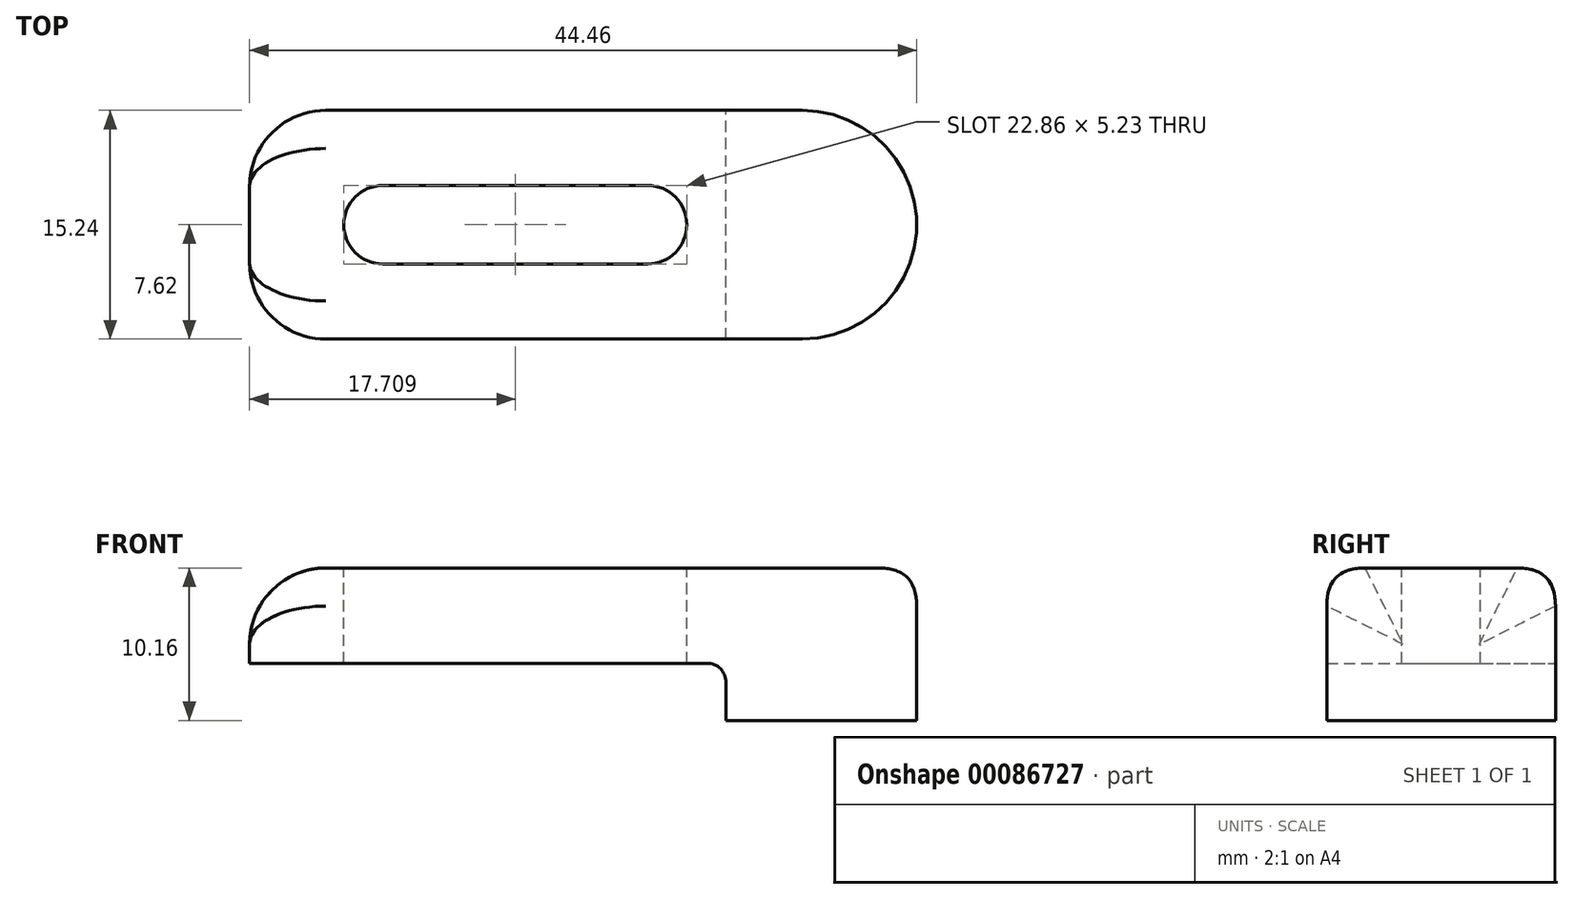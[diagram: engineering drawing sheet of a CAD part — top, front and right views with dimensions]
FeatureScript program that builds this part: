
annotation { "Feature Type Name" : "Feature", "Feature Type Description" : "" }
export const myFeature = defineFeature(function(context is Context, id is Id, definition is map)
    precondition{}
    {
        {
            var Q0;
            Q0=qCreatedBy(makeId("Top.planeOp"),FACE);
            var sketch = newSketch(context, id + "F0", { "sketchPlane" : qUnion([Q0])});
            skLineSegment(sketch, "E0.bottom", {"start": v(14.6, -7.62) * mm, "end": v(-22.23, -7.62) * mm});
            skLineSegment(sketch, "E0.top", {"start": v(14.6, 7.62) * mm, "end": v(-22.23, 7.62) * mm});
            skLineSegment(sketch, "E0.left", {"start": v(22.23, 0) * mm, "end": v(22.23, 0) * mm});
            skLineSegment(sketch, "E0.right", {"start": v(-22.23, -7.62) * mm, "end": v(-22.23, 7.62) * mm});
            skPoint(sketch, "E0.middle", {"position": v(0, 0) * mm});
            skPoint(sketch, "E1.visualSharp", {"position": v(22.23, 7.62) * mm});
            skArc(sketch, "E1.filletArc", {"start": v(22.23, 0) * mm, "mid": v(20, 5.39) * mm, "end": v(14.6, 7.62) * mm});
            skPoint(sketch, "E2.visualSharp", {"position": v(22.23, -7.62) * mm});
            skArc(sketch, "E2.filletArc", {"start": v(14.6, -7.62) * mm, "mid": v(20, -5.39) * mm, "end": v(22.23, 0) * mm});
            skSolve(sketch);
        }
        {
            var Q0;
            Q0=qSketchRegion(id+"F0",true);
            extrude(context, id + "F1", {"entities" : qUnion([Q0]), "depth" : 10.16 * mm});
        }
        {
            var Q0;
            Q0=makeQuery(id+"F1.opExtrude","CAP_FACE",FACE,{"disambiguationData":[OSD([sQuery(id+"F0.wireOp",EDGE,"E0.bottom"),sQuery(id+"F0.wireOp",EDGE,"E0.top"),sQuery(id+"F0.wireOp",EDGE,"E0.right"),sQuery(id+"F0.wireOp",EDGE,"E1.filletArc"),sQuery(id+"F0.wireOp",EDGE,"E2.filletArc")])],"isStart":true});
            var sketch = newSketch(context, id + "F2", { "sketchPlane" : qUnion([Q0])});
            skLineSegment(sketch, "E3.bottom", {"start": v(-22.23, 7.62) * mm, "end": v(9.53, 7.62) * mm});
            skLineSegment(sketch, "E3.top", {"start": v(-22.23, -7.62) * mm, "end": v(9.53, -7.62) * mm});
            skLineSegment(sketch, "E3.left", {"start": v(-22.23, 7.62) * mm, "end": v(-22.23, -7.62) * mm});
            skLineSegment(sketch, "E3.right", {"start": v(9.53, 7.62) * mm, "end": v(9.53, -7.62) * mm});
            skSolve(sketch);
        }
        {
            var Q0;
            Q0=qSketchRegion(id+"F2",true);
            extrude(context, id + "F3", {"entities" : qUnion([Q0]), "operationType" : NewBodyOperationType.REMOVE, "oppositeDirection" : true, "depth" : 3.8 * mm});
        }
        {
            var Q0;
            Q0=makeQuery(id+"F1.opExtrude","CAP_EDGE",EDGE,{"disambiguationData":[OSD([sQuery(id+"F0.wireOp",EDGE,"E0.bottom")])],"isStart":false});
            fillet(context, id + "F4", {"entities" : qUnion([Q0]), "radius" : 2.54 * mm, "tangentPropagation" : true, "rho" : 0.5, "crossSection" : FilletCrossSection.CONIC, "allowEdgeOverflow" : false});
        }
        {
            var Q0;
            Q0=makeQuery(id+"F3.boolean.opBoolean","COPY",EDGE,{"derivedFrom":makeQuery(id+"F3.opExtrude","CAP_EDGE",EDGE,{"disambiguationData":[OSD([sQuery(id+"F2.wireOp",EDGE,"E3.right")])],"isStart":false})});
            var Q1;
            Q1=makeQuery(id+"F3.boolean.opBoolean","COPY",EDGE,{"derivedFrom":makeQuery(id+"F3.opExtrude","CAP_EDGE",EDGE,{"disambiguationData":[OSD([sQuery(id+"F2.wireOp",EDGE,"E3.right")])],"isStart":true})});
            fillet(context, id + "F5", {"entities" : qUnion([Q0, Q1]), "radius" : 1.27 * mm, "tangentPropagation" : true, "allowEdgeOverflow" : false});
        }
        {
            var Q0;
            Q0=makeQuery(id+"F1.opExtrude","CAP_FACE",FACE,{"disambiguationData":[OSD([sQuery(id+"F0.wireOp",EDGE,"E0.bottom"),sQuery(id+"F0.wireOp",EDGE,"E0.top"),sQuery(id+"F0.wireOp",EDGE,"E0.right"),sQuery(id+"F0.wireOp",EDGE,"E1.filletArc"),sQuery(id+"F0.wireOp",EDGE,"E2.filletArc")])],"isStart":false});
            var sketch = newSketch(context, id + "F6", { "sketchPlane" : qUnion([Q0])});
            skLineSegment(sketch, "E4.bottom", {"start": v(4.3, -2.62) * mm, "end": v(-13.34, -2.62) * mm});
            skLineSegment(sketch, "E4.top", {"start": v(4.3, 2.62) * mm, "end": v(-13.34, 2.62) * mm});
            skLineSegment(sketch, "E4.left", {"start": v(6.9, 0) * mm, "end": v(6.9, 0) * mm});
            skLineSegment(sketch, "E4.right", {"start": v(-15.95, 0) * mm, "end": v(-15.95, 0) * mm});
            skPoint(sketch, "E4.middle", {"position": v(-4.52, 0) * mm});
            skPoint(sketch, "E4.middle.positionSnap0", {"position": v(-22.23, 0) * mm});
            skPoint(sketch, "E4.centerSnap0", {"position": v(-22.23, 0) * mm});
            skPoint(sketch, "E5.visualSharp", {"position": v(-15.95, 2.62) * mm});
            skArc(sketch, "E5.filletArc", {"start": v(-13.34, 2.62) * mm, "mid": v(-15.18, 1.85) * mm, "end": v(-15.95, 0) * mm});
            skPoint(sketch, "E6.visualSharp", {"position": v(-15.95, -2.62) * mm});
            skArc(sketch, "E6.filletArc", {"start": v(-15.95, 0) * mm, "mid": v(-15.18, -1.85) * mm, "end": v(-13.34, -2.62) * mm});
            skPoint(sketch, "E7.visualSharp", {"position": v(6.9, -2.62) * mm});
            skArc(sketch, "E7.filletArc", {"start": v(4.3, -2.62) * mm, "mid": v(6.14, -1.85) * mm, "end": v(6.9, 0) * mm});
            skPoint(sketch, "E8.visualSharp", {"position": v(6.9, 2.62) * mm});
            skArc(sketch, "E8.filletArc", {"start": v(6.9, 0) * mm, "mid": v(6.14, 1.85) * mm, "end": v(4.3, 2.62) * mm});
            skSolve(sketch);
        }
        {
            var Q0;
            Q0=qSketchRegion(id+"F6",true);
            extrude(context, id + "F7", {"entities" : qUnion([Q0]), "operationType" : NewBodyOperationType.REMOVE, "endBound" : BoundingType.UP_TO_NEXT, "oppositeDirection" : true, "depth" : 25.4 * mm});
        }
        {
            var Q0;
            Q0=makeQuery(id+"F1.opExtrude","CAP_EDGE",EDGE,{"disambiguationData":[OSD([sQuery(id+"F0.wireOp",EDGE,"E0.right")])],"isStart":false});
            var Q1;
            {var subQ0=sQuery(id+"F0.wireOp",EDGE,"E0.top");Q1=makeQuery(id+"F4.opFillet","BLEND_EDGE",EDGE,{"blendedFrom":[makeQuery(id+"F1.opExtrude","CAP_EDGE",EDGE,{"disambiguationData":[OSD([subQ0])],"isStart":false}),makeQuery(id+"F1.opExtrude","SWEPT_FACE",FACE,{"disambiguationData":[OSD([subQ0])]})],"blendedInto":[makeQuery(id+"F1.opExtrude","SWEPT_FACE",FACE,{"disambiguationData":[OSD([subQ0])]})]});}
            fillet(context, id + "F8", {"entities" : qUnion([Q0, Q1]), "radius" : 5.08 * mm, "tangentPropagation" : true, "allowEdgeOverflow" : false});
        }
    });
